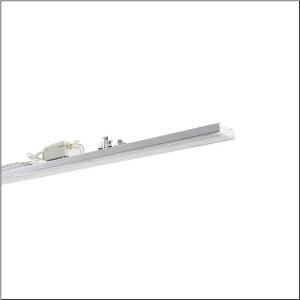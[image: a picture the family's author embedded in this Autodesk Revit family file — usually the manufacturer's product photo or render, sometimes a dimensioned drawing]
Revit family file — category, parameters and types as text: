
# Revit family: licross_21_recessed_mo_52te10cn49xg
name_source: partatom
category: Lighting Fixtures
units: mm (PartAtom-declared; Revit-internal decimal feet)

## family parameters
Cut with Voids When Loaded = No
Host = Face
Light Source = No
Part Type = Normal
Room Calculation Point = No
Round Connector Dimension = Use Diameter
Shared = No

## types (1)
- --- (1 x LED, 9010 lm, 49.9 W, 4000K)
    Apparent Load = 50 VA
    CIE Flux Codes = 50 81 96 100 100
    Color Rendering = 80
    Color Temperature = 4000K
    Default Elevation = 1800 mm
    Description = Licross 21 Recessed MO, luminaire insert, of sheet steel, galvanised, coil coated, white, length: 1.500mm, width: 66mm, height: 67mm, LED rated luminous flux: 9.010lm, light colour: 840, SDCM (Standard Deviation of Colour Matching)MacAdam ≤ 3 SDCM (initial), control gear: ON/OFF Multilumen, CLOi, with plug, 3-pole, with phase selection, mains connection: 220..240V, AC, 50/60Hz, start of lifetime: 49W, end of service life: 61W, internal wiring halogen-free, primary optical cover: cover, of PMMA, light emission: direct distribution, primary light characteristic: symmetric, protection rating (complete): IP54, insulation class (complete): insulation class I (protective earthing), certification: CE, ENEC, VDE, UKCA, protection symbol: D if used in an environment with non-conductive dust loads with corresponding accessories, impact resistance: IK06, permissible ambient temperature for indoor applications: -35..+40°C, corresponds to IFS (International Featured Standards) requirements for safety and quality in the food industry, reducing of maximum allowable ambient temperature of 5°C with ceiling mounting, LABS conformity tested according to VDMA 24364:2018-05, The light source and the operating device comply with the requirements of the Ecodesign Regulation (EU) 2019/2020 and are replaceable in accordance with this regulation, packaging unit: 1 piece
    Height = 58 mm
    Lamp = 1 x LED
    Lamp Light Flux = 9010 lm
    Lamp Power = 49.9 W
    Lamp count = 1
    Length = 1500 mm
    Luminous efficacy = 181 lm/W
    Manufacturer = Siteco
    ModVariant = No
    Model = 52TE10CN49XG
    Mounting Place = Ceiling
    Mounting Type = Pendant
    Number of Poles = 1
    OnlyDefault = Yes
    Power Factor = 1
    Product Name = Licross 21 Recessed MO
    Product group = luminaire insert | ceiling pendant
    ProductGroupID = 901
    Protection Class = Protection class I
    Protection Degree = IP 54
    RLX_Detail_Level = 1
    RLX_Emergency_Light_Flux = 0 lm
    RLX_Emergency_Type = 0
    RLX_Emergency_Type_DB = No
    RlxData = <blob elided: 22409 chars, md5=1582ab85>
    Socket = socket
    Standby Power = 0 W
    System Light Flux = 9010 lm
    System Power = 50 W
    Type Comments = factory setting: luminous flux: 100 % | (A | C | E) | 116 mA
    Type Image = l_1296930.jpg
    URL = http://relux.com
    VarID = @adj_112237
    Voltage = 0 V
    Weight = 0.00 kg
    Width = 66 mm

## geometry (parser evidence)
native form markers: Blend x4, Sweep x10
no freeform markers — native parametric forms only
